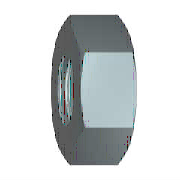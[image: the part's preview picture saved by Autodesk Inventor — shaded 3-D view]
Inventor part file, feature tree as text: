
AUTODESK INVENTOR PART (.ipt)
format: ipt  version: 2022.1 (Build 261234000, 234)  size: 165,888 bytes
history: native  units: mm (DEFAULTED — no unit token found)
features: sketch x3, extrude x1, chamfer x1, hole x1, other x1, plane x1
ambient origin geometry x7: Origin, YZ Plane, XZ Plane, X Axis, Y Axis, Z Axis, Center Point
bodies: Solid1 (feature_tree)
feature tree (8):
  extrude  "Cuerpo"  Depth=12.8mm
  chamfer  "Chaflán1"  Angle=30.0deg  [1 undecoded]
  hole  "Rosca"  [1 undecoded]
  other  "Work Axis1"
  plane  "Work Plane1"
  sketch  "Boceto1"  dims[d0=24.248711mm d1=12.8mm]
  sketch  "Boceto2"  dims[d2=0.0mm]
  sketch  "Boceto3"  dims[d3=30.0deg d4=30.0deg d5=19.6mm d6=19.6mm d7=90.0deg d25=11.835mm d26=6.0mm d27=4.0mm d28=2.0mm d29=14.3117mm d30=8.0mm d31=20.594885mm d8=1.082532mm d9=30.0deg d10=1.082532mm d11=30.0deg d13=0.0mm d14=0.0mm d39=0.0mm d40=1.082532mm d41=1.082532mm d42=0.0mm]
note: 2 required parameter values undecoded (feature->parameter linkage not recoverable at this tier; creation-order binding heuristic only, values carry confidence <= 0.55)
